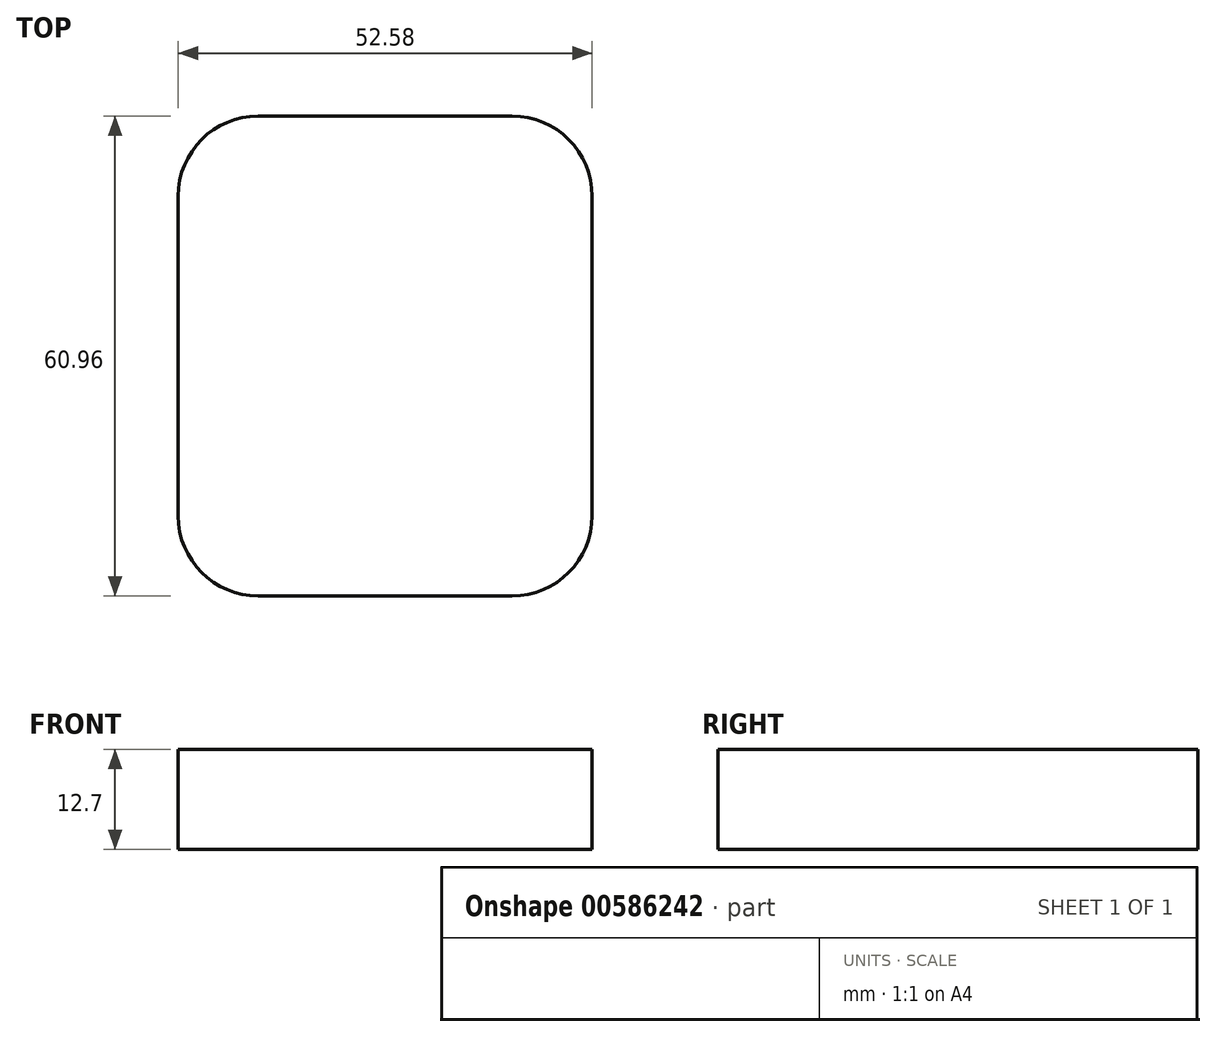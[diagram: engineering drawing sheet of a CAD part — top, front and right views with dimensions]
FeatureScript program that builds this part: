
annotation { "Feature Type Name" : "Feature", "Feature Type Description" : "" }
export const myFeature = defineFeature(function(context is Context, id is Id, definition is map)
    precondition{}
    {
        {
            var Q0;
            Q0=qCreatedBy(makeId("Top.planeOp"),FACE);
            var sketch = newSketch(context, id + "F0", { "sketchPlane" : qUnion([Q0])});
            skLineSegment(sketch, "E0.bottom", {"start": v(0, 0) * mm, "end": v(52.58, 0) * mm});
            skLineSegment(sketch, "E0.top", {"start": v(0, 60.96) * mm, "end": v(52.58, 60.96) * mm});
            skLineSegment(sketch, "E0.left", {"start": v(0, 0) * mm, "end": v(0, 60.96) * mm});
            skLineSegment(sketch, "E0.right", {"start": v(52.58, 0) * mm, "end": v(52.58, 60.96) * mm});
            skSolve(sketch);
        }
        {
            var Q0;
            Q0=makeQuery(id+"F0.imprint","IMPRINT",FACE,{"disambiguationData":[TD([[makeQuery(id+"F0.imprint","IMPRINT",EDGE,{"derivedFrom":sQuery(id+"F0.wireOp",EDGE,"E0.bottom")}),1.0]])]});
            extrude(context, id + "F1", {"entities" : qUnion([Q0]), "depth" : 12.7 * mm, "offsetDistance" : 25.4 * mm});
        }
        {
            var Q0;
            Q0=makeQuery(id+"F1.opExtrude","SWEPT_EDGE",EDGE,{"disambiguationData":[OSD([sQuery(id+"F0.wireOp",EDGE,"E0.top"),sQuery(id+"F0.wireOp",EDGE,"E0.left")])]});
            var Q1;
            Q1=makeQuery(id+"F1.opExtrude","SWEPT_EDGE",EDGE,{"disambiguationData":[OSD([sQuery(id+"F0.wireOp",EDGE,"E0.bottom"),sQuery(id+"F0.wireOp",EDGE,"E0.left")])]});
            var Q2;
            Q2=makeQuery(id+"F1.opExtrude","SWEPT_EDGE",EDGE,{"disambiguationData":[OSD([sQuery(id+"F0.wireOp",EDGE,"E0.bottom"),sQuery(id+"F0.wireOp",EDGE,"E0.right")])]});
            var Q3;
            Q3=makeQuery(id+"F1.opExtrude","SWEPT_EDGE",EDGE,{"disambiguationData":[OSD([sQuery(id+"F0.wireOp",EDGE,"E0.top"),sQuery(id+"F0.wireOp",EDGE,"E0.right")])]});
            fillet(context, id + "F2", {"entities" : qUnion([Q0, Q1, Q2, Q3]), "radius" : 10.16 * mm, "tangentPropagation" : true, "allowEdgeOverflow" : false});
        }
    });
